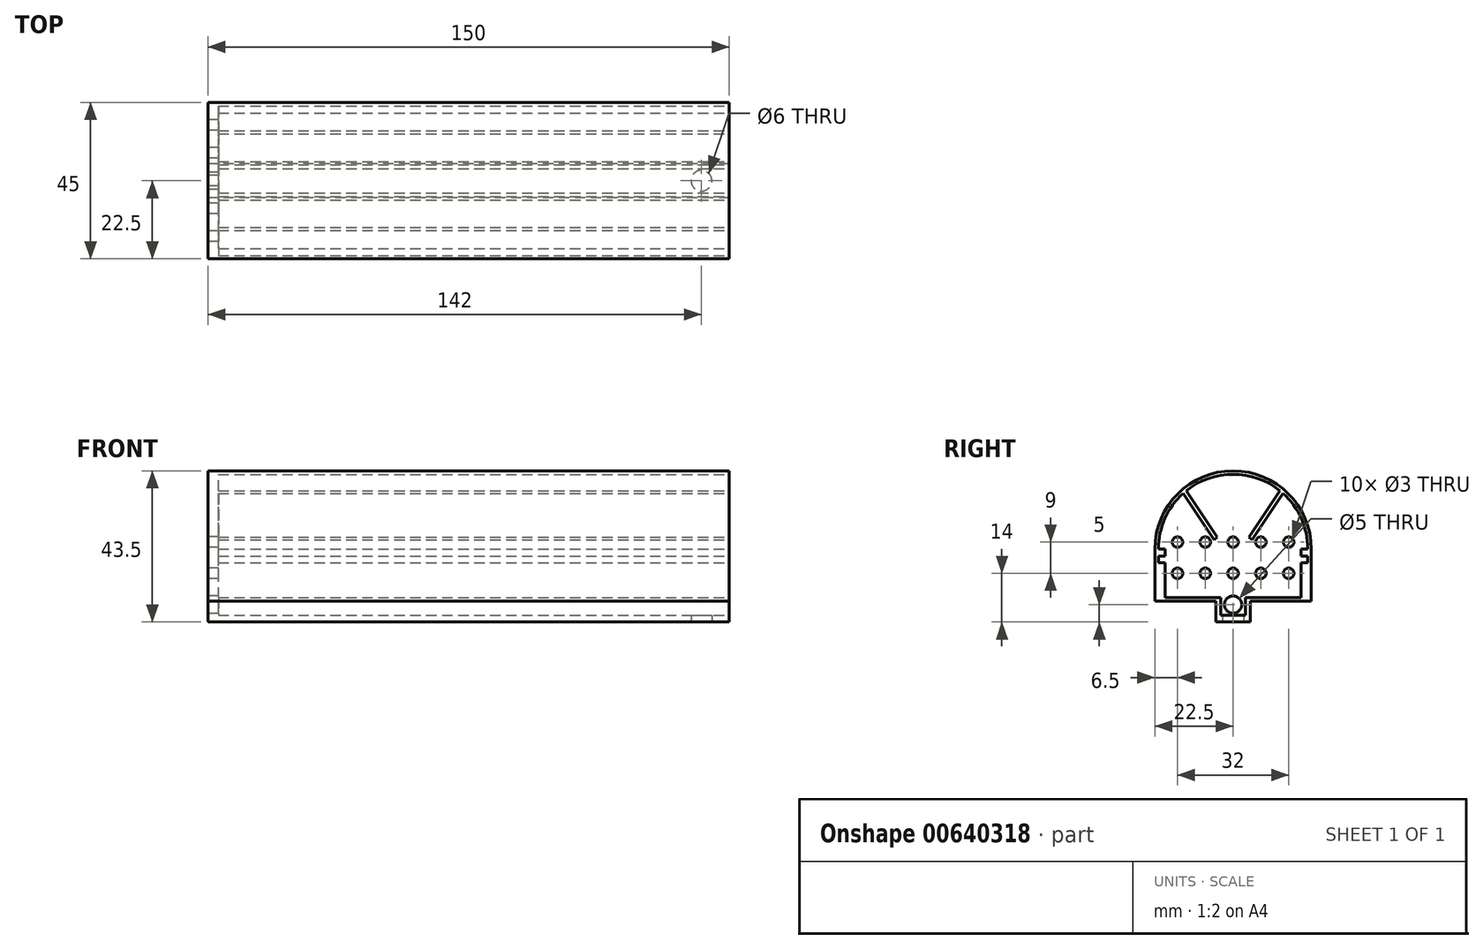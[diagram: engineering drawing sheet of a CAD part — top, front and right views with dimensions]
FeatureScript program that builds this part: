
annotation { "Feature Type Name" : "Feature", "Feature Type Description" : "" }
export const myFeature = defineFeature(function(context is Context, id is Id, definition is map)
    precondition{}
    {
        {
            var Q0;
            Q0=qCreatedBy(makeId("Right.planeOp"),FACE);
            var sketch = newSketch(context, id + "F0", { "sketchPlane" : qUnion([Q0])});
            skLineSegment(sketch, "E0", {"start": v(-22.5, 0) * mm, "end": v(-4.9, 0) * mm});
            skLineSegment(sketch, "E1", {"start": v(22.5, 0) * mm, "end": v(22.5, 15) * mm});
            skLineSegment(sketch, "E2.MirrorCS", {"start": v(-22.5, 0) * mm, "end": v(-22.5, 15) * mm});
            skArc(sketch, "E3", {"start": v(22.5, 15) * mm, "mid": v(0, 37.5) * mm, "end": v(-22.5, 15) * mm});
            skLineSegment(sketch, "E4", {"start": v(-4.9, 0) * mm, "end": v(-4.9, -6) * mm});
            skLineSegment(sketch, "E5", {"start": v(-4.9, -6) * mm, "end": v(4.9, -6) * mm});
            skLineSegment(sketch, "E6", {"start": v(4.9, -6) * mm, "end": v(4.9, 0) * mm});
            skLineSegment(sketch, "E7.trimOffspring", {"start": v(4.9, 0) * mm, "end": v(22.5, 0) * mm});
            skSolve(sketch);
        }
        {
            var Q0;
            Q0 = qSketchRegion(id + "F0", true);
            extrude(context, id + "F1", {"entities" : qUnion([Q0]), "depth" : 150 * mm, "offsetDistance" : 25 * mm});
        }
        {
            var Q0;
            Q0=makeQuery(id+"F1.opExtrude","CAP_FACE",FACE,{"disambiguationData":[OSD([sQuery(id+"F0.wireOp",EDGE,"E0"),sQuery(id+"F0.wireOp",EDGE,"E1"),sQuery(id+"F0.wireOp",EDGE,"E2.MirrorCS"),sQuery(id+"F0.wireOp",EDGE,"E3"),sQuery(id+"F0.wireOp",EDGE,"E4"),sQuery(id+"F0.wireOp",EDGE,"E5"),sQuery(id+"F0.wireOp",EDGE,"E6"),sQuery(id+"F0.wireOp",EDGE,"E7.trimOffspring")])],"isStart":false});
            var sketch = newSketch(context, id + "F2", { "sketchPlane" : qUnion([Q0])});
            skLineSegment(sketch, "E8", {"start": v(-19.5, 1) * mm, "end": v(-3.5, 1) * mm});
            skLineSegment(sketch, "E9", {"start": v(-3.5, 1) * mm, "end": v(-3.5, -4) * mm});
            skLineSegment(sketch, "E10", {"start": v(-3.5, -4) * mm, "end": v(3.5, -4) * mm});
            skLineSegment(sketch, "E11", {"start": v(3.5, -4) * mm, "end": v(3.5, 1) * mm});
            skLineSegment(sketch, "E12", {"start": v(3.5, 1) * mm, "end": v(19.5, 1) * mm});
            skLineSegment(sketch, "E13", {"start": v(19.5, 1) * mm, "end": v(19.5, 11) * mm});
            skLineSegment(sketch, "E14", {"start": v(19.5, 11) * mm, "end": v(21.5, 11) * mm});
            skLineSegment(sketch, "E15", {"start": v(21.5, 11) * mm, "end": v(21.5, 13) * mm});
            skLineSegment(sketch, "E16", {"start": v(21.5, 13) * mm, "end": v(19.5, 13) * mm});
            skLineSegment(sketch, "E17", {"start": v(19.5, 13) * mm, "end": v(19.5, 15) * mm});
            skLineSegment(sketch, "E18", {"start": v(19.5, 15) * mm, "end": v(21.5, 15) * mm});
            skLineSegment(sketch, "E19.MirrorCS", {"start": v(-19.5, 1) * mm, "end": v(-19.5, 11) * mm});
            skLineSegment(sketch, "E20.MirrorCS", {"start": v(-19.5, 11) * mm, "end": v(-21.5, 11) * mm});
            skLineSegment(sketch, "E21.MirrorCS", {"start": v(-21.5, 11) * mm, "end": v(-21.5, 13) * mm});
            skLineSegment(sketch, "E22.MirrorCS", {"start": v(-21.5, 13) * mm, "end": v(-19.5, 13) * mm});
            skLineSegment(sketch, "E23.MirrorCS", {"start": v(-19.5, 13) * mm, "end": v(-19.5, 15) * mm});
            skLineSegment(sketch, "E24.MirrorCS", {"start": v(-19.5, 15) * mm, "end": v(-21.5, 15) * mm});
            skArc(sketch, "E25", {"start": v(21.5, 15) * mm, "mid": v(19.63, 23.76) * mm, "end": v(14.36, 31) * mm});
            skLineSegment(sketch, "E26", {"start": v(-14.36, 31) * mm, "end": v(-5.5, 17.68) * mm});
            skLineSegment(sketch, "E27", {"start": v(-5.5, 17.68) * mm, "end": v(-4.58, 18.46) * mm});
            skLineSegment(sketch, "E28", {"start": v(-4.58, 18.46) * mm, "end": v(-13.44, 31.78) * mm});
            skArc(sketch, "E29.trimOffspring", {"start": v(-14.36, 31) * mm, "mid": v(-19.63, 23.76) * mm, "end": v(-21.5, 15) * mm});
            skLineSegment(sketch, "E30.MirrorCS", {"start": v(4.58, 18.46) * mm, "end": v(13.44, 31.78) * mm});
            skLineSegment(sketch, "E31.MirrorCS", {"start": v(5.5, 17.68) * mm, "end": v(4.58, 18.46) * mm});
            skLineSegment(sketch, "E32.MirrorCS", {"start": v(14.36, 31) * mm, "end": v(5.5, 17.68) * mm});
            skArc(sketch, "E33.trimOffspring", {"start": v(13.44, 31.78) * mm, "mid": v(0, 36.5) * mm, "end": v(-13.44, 31.78) * mm});
            skSolve(sketch);
        }
        {
            var Q0;
            Q0 = qSketchRegion(id + "F2", true);
            extrude(context, id + "F3", {"entities" : qUnion([Q0]), "operationType" : NewBodyOperationType.REMOVE, "oppositeDirection" : true, "depth" : 147 * mm, "offsetDistance" : 25 * mm});
        }
        {
            var Q0;
            Q0=makeQuery(id+"F1.opExtrude","CAP_FACE",FACE,{"disambiguationData":[OSD([sQuery(id+"F0.wireOp",EDGE,"E0"),sQuery(id+"F0.wireOp",EDGE,"E1"),sQuery(id+"F0.wireOp",EDGE,"E2.MirrorCS"),sQuery(id+"F0.wireOp",EDGE,"E3"),sQuery(id+"F0.wireOp",EDGE,"E4"),sQuery(id+"F0.wireOp",EDGE,"E5"),sQuery(id+"F0.wireOp",EDGE,"E6"),sQuery(id+"F0.wireOp",EDGE,"E7.trimOffspring")])],"isStart":true});
            var sketch = newSketch(context, id + "F4", { "sketchPlane" : qUnion([Q0])});
            skCircle(sketch, "E34", {"center": v(0, -1) * mm, "radius": 2.5 * mm});
            skSolve(sketch);
        }
        {
            var Q0;
            Q0 = qSketchRegion(id + "F4", true);
            extrude(context, id + "F5", {"entities" : qUnion([Q0]), "operationType" : NewBodyOperationType.REMOVE, "endBound" : BoundingType.UP_TO_NEXT, "oppositeDirection" : true, "depth" : 25 * mm, "offsetDistance" : 25 * mm});
        }
        {
            var Q0;
            Q0=makeQuery(id+"F4.imprint","IMPRINT",FACE,{"disambiguationData":[TD([[makeQuery(id+"F4.imprint","IMPRINT",EDGE,{"derivedFrom":sQuery(id+"F4.wireOp",EDGE,"E34")}),-1.0]])]});
            var sketch = newSketch(context, id + "F6", { "sketchPlane" : qUnion([Q0])});
            skCircle(sketch, "E35", {"center": v(-16, 8) * mm, "radius": 1.5 * mm});
            skCircle(sketch, "E36.0.1.0", {"center": v(-16, 17) * mm, "radius": 1.5 * mm});
            skCircle(sketch, "E36.1.0.0", {"center": v(-8, 8) * mm, "radius": 1.5 * mm});
            skCircle(sketch, "E36.1.1.0", {"center": v(-8, 17) * mm, "radius": 1.5 * mm});
            skCircle(sketch, "E36.2.0.0", {"center": v(0, 8) * mm, "radius": 1.5 * mm});
            skCircle(sketch, "E36.2.1.0", {"center": v(0, 17) * mm, "radius": 1.5 * mm});
            skCircle(sketch, "E36.3.0.0", {"center": v(8, 8) * mm, "radius": 1.5 * mm});
            skCircle(sketch, "E36.3.1.0", {"center": v(8, 17) * mm, "radius": 1.5 * mm});
            skCircle(sketch, "E36.4.0.0", {"center": v(16, 8) * mm, "radius": 1.5 * mm});
            skCircle(sketch, "E36.4.1.0", {"center": v(16, 17) * mm, "radius": 1.5 * mm});
            skLineSegment(sketch, "E36.direction1", {"start": v(-16, 8) * mm, "end": v(-8, 8) * mm, "construction": true});
            skLineSegment(sketch, "E36.direction2", {"start": v(-16, 8) * mm, "end": v(-16, 17) * mm, "construction": true});
            skSolve(sketch);
        }
        {
            var Q0;
            Q0 = qSketchRegion(id + "F6", true);
            extrude(context, id + "F7", {"entities" : qUnion([Q0]), "operationType" : NewBodyOperationType.REMOVE, "endBound" : BoundingType.UP_TO_NEXT, "oppositeDirection" : true, "depth" : 25 * mm, "offsetDistance" : 25 * mm});
        }
        {
            var Q0;
            Q0=makeQuery(id+"F1.opExtrude","SWEPT_FACE",FACE,{"disambiguationData":[OSD([sQuery(id+"F0.wireOp",EDGE,"E5")])]});
            var sketch = newSketch(context, id + "F8", { "sketchPlane" : qUnion([Q0])});
            skCircle(sketch, "E37", {"center": v(142, 0) * mm, "radius": 3 * mm});
            skPoint(sketch, "E37.centerSnap0", {"position": v(150, 0) * mm});
            skSolve(sketch);
        }
        {
            var Q0;
            Q0=makeQuery(id+"F8.imprint","IMPRINT",FACE,{"disambiguationData":[TD([[makeQuery(id+"F8.imprint","IMPRINT",EDGE,{"derivedFrom":sQuery(id+"F8.wireOp",EDGE,"E37")}),1.0]])]});
            extrude(context, id + "F9", {"entities" : qUnion([Q0]), "operationType" : NewBodyOperationType.REMOVE, "endBound" : BoundingType.UP_TO_NEXT, "oppositeDirection" : true, "depth" : 25 * mm, "offsetDistance" : 25 * mm});
        }
    });
